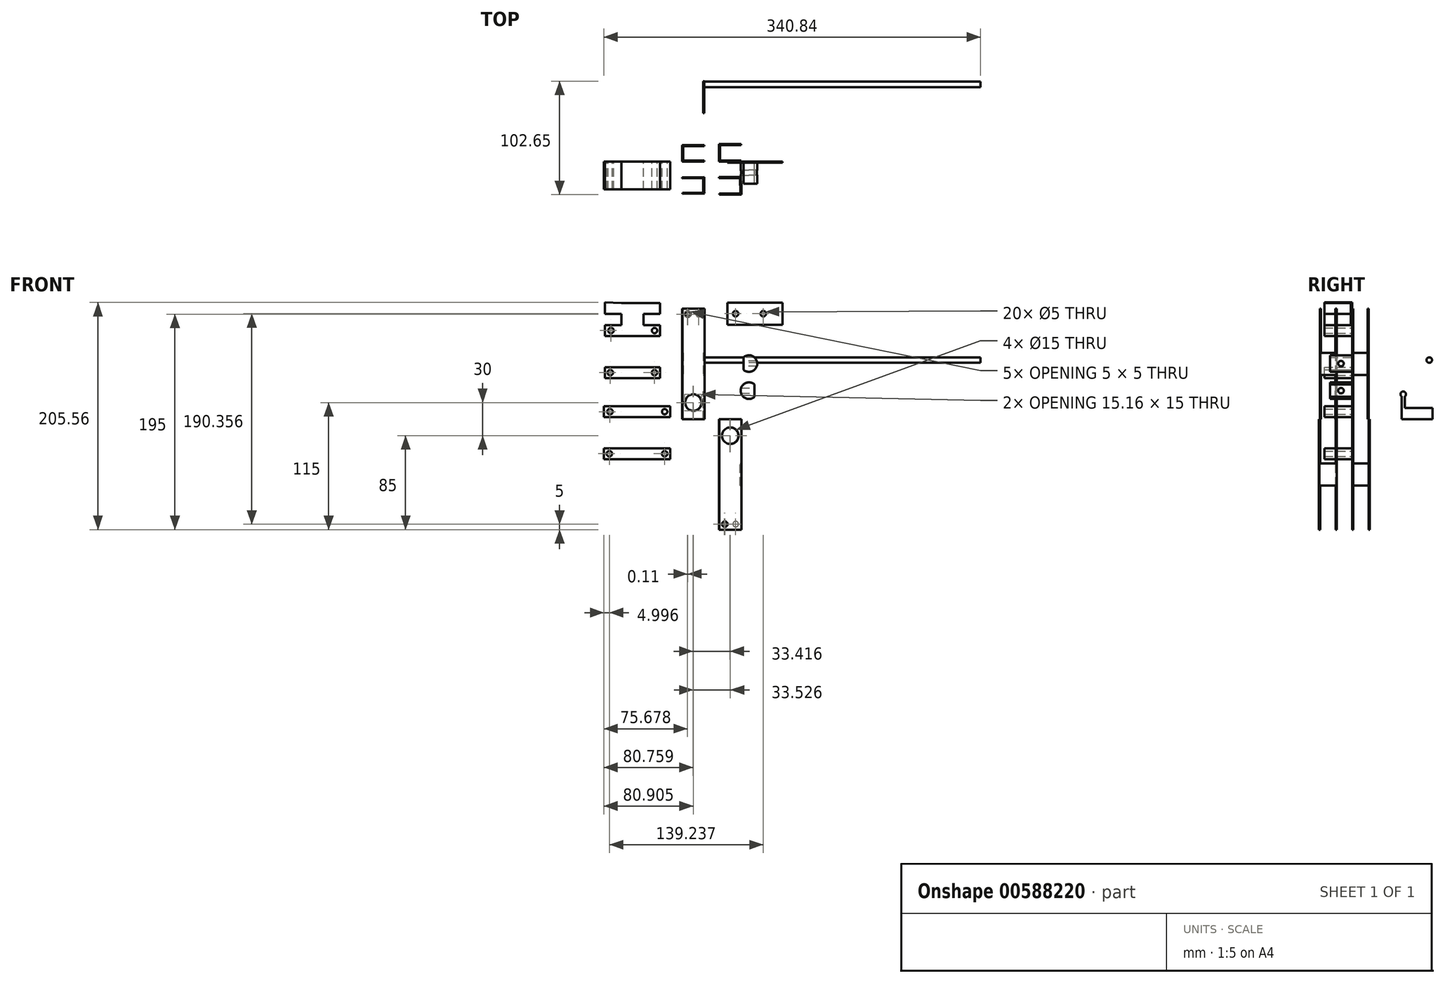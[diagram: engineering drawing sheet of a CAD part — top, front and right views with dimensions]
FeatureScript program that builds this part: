
annotation { "Feature Type Name" : "Feature", "Feature Type Description" : "" }
export const myFeature = defineFeature(function(context is Context, id is Id, definition is map)
    precondition{}
    {
        {
            var Q0;
            Q0=qCreatedBy(makeId("Top.planeOp"),FACE);
            var sketch = newSketch(context, id + "F0", { "sketchPlane" : qUnion([Q0])});
            skLineSegment(sketch, "E0", {"start": v(0, 15) * mm, "end": v(-20, 15) * mm});
            skLineSegment(sketch, "E1", {"start": v(-20, 15) * mm, "end": v(-20, 0) * mm});
            skLineSegment(sketch, "E2", {"start": v(-20, 0) * mm, "end": v(0, 0) * mm});
            skLineSegment(sketch, "E3", {"start": v(0, 0) * mm, "end": v(0, 1) * mm});
            skLineSegment(sketch, "E4", {"start": v(0, 1) * mm, "end": v(-19, 1) * mm});
            skLineSegment(sketch, "E5", {"start": v(-19, 1) * mm, "end": v(-19, 14) * mm});
            skLineSegment(sketch, "E6", {"start": v(-19, 14) * mm, "end": v(0, 14) * mm});
            skLineSegment(sketch, "E7", {"start": v(0, 14) * mm, "end": v(0, 15) * mm});
            skLineSegment(sketch, "E8", {"start": v(33.42, 1) * mm, "end": v(14.42, 1) * mm});
            skLineSegment(sketch, "E9", {"start": v(14.42, 1) * mm, "end": v(14.42, 15) * mm});
            skLineSegment(sketch, "E10", {"start": v(14.42, 15) * mm, "end": v(33.42, 15) * mm});
            skLineSegment(sketch, "E11", {"start": v(33.42, 15) * mm, "end": v(33.42, 16) * mm});
            skLineSegment(sketch, "E12", {"start": v(33.42, 16) * mm, "end": v(13.42, 16) * mm});
            skLineSegment(sketch, "E13", {"start": v(13.42, 16) * mm, "end": v(13.42, 0) * mm});
            skLineSegment(sketch, "E14", {"start": v(13.42, 0) * mm, "end": v(33.42, 0) * mm});
            skLineSegment(sketch, "E15", {"start": v(33.42, 0) * mm, "end": v(33.42, 1) * mm});
            skLineSegment(sketch, "E16", {"start": v(-36.62, -7.13) * mm, "end": v(38.64, -6.85) * mm, "construction": true});
            skLineSegment(sketch, "E17.MirrorCS", {"start": v(-19, 16) * mm, "end": v(0, 16) * mm});
            skLineSegment(sketch, "E18.MirrorCS", {"start": v(-19.95, -14.13) * mm, "end": v(0.05, -13.99) * mm});
            skLineSegment(sketch, "E19.MirrorCS", {"start": v(0.16, -28.99) * mm, "end": v(-19.84, -29.13) * mm});
            skLineSegment(sketch, "E20.MirrorCS", {"start": v(13.47, -13.89) * mm, "end": v(33.47, -13.74) * mm});
            skLineSegment(sketch, "E21.MirrorCS", {"start": v(33.58, -29.74) * mm, "end": v(13.58, -29.89) * mm});
            skLineSegment(sketch, "E22", {"start": v(13.47, -13.89) * mm, "end": v(13.47, -14.89) * mm});
            skLineSegment(sketch, "E23", {"start": v(13.47, -14.89) * mm, "end": v(32.47, -14.75) * mm});
            skLineSegment(sketch, "E24", {"start": v(32.58, -28.75) * mm, "end": v(13.58, -28.89) * mm});
            skLineSegment(sketch, "E25", {"start": v(13.58, -28.89) * mm, "end": v(13.58, -29.89) * mm});
            skLineSegment(sketch, "E26", {"start": v(32.58, -28.75) * mm, "end": v(32.47, -14.75) * mm});
            skLineSegment(sketch, "E27", {"start": v(33.47, -13.74) * mm, "end": v(33.58, -29.74) * mm});
            skLineSegment(sketch, "E28", {"start": v(0.05, -13.99) * mm, "end": v(0.16, -28.99) * mm});
            skLineSegment(sketch, "E29", {"start": v(-19.95, -14.13) * mm, "end": v(-19.94, -15.13) * mm});
            skLineSegment(sketch, "E30", {"start": v(-19.94, -15.13) * mm, "end": v(-0.94, -15) * mm});
            skLineSegment(sketch, "E31", {"start": v(-0.94, -15) * mm, "end": v(-0.85, -28) * mm});
            skLineSegment(sketch, "E32", {"start": v(-0.85, -28) * mm, "end": v(-19.84, -28.13) * mm});
            skLineSegment(sketch, "E33", {"start": v(-19.84, -29.13) * mm, "end": v(-19.84, -28.13) * mm});
            skSolve(sketch);
        }
        {
            var Q0;
            Q0=makeQuery(id+"F0.imprint","IMPRINT",FACE,{"disambiguationData":[TD([[makeQuery(id+"F0.imprint","IMPRINT",EDGE,{"derivedFrom":sQuery(id+"F0.wireOp",EDGE,"E0")}),1.0]])]});
            var Q1;
            Q1=makeQuery(id+"F0.imprint","IMPRINT",FACE,{"disambiguationData":[TD([[makeQuery(id+"F0.imprint","IMPRINT",EDGE,{"derivedFrom":sQuery(id+"F0.wireOp",EDGE,"E19.MirrorCS")}),-1.0]])]});
            extrude(context, id + "F1", {"entities" : qUnion([Q0, Q1]), "depth" : 100 * mm, "offsetDistance" : 25 * mm});
        }
        {
            var Q0;
            Q0=makeQuery(id+"F1.opExtrude","SWEPT_FACE",FACE,{"disambiguationData":[OSD([sQuery(id+"F0.wireOp",EDGE,"E2")])]});
            var sketch = newSketch(context, id + "F2", { "sketchPlane" : qUnion([Q0])});
            skCircle(sketch, "E34", {"center": v(-10, 15) * mm, "radius": 7.5 * mm});
            skPoint(sketch, "E34.centerSnap0", {"position": v(-10, 0) * mm});
            skCircle(sketch, "E35", {"center": v(-5, 95) * mm, "radius": 2.5 * mm});
            skSolve(sketch);
        }
        {
            var Q0;
            Q0=makeQuery(id+"F2.imprint","IMPRINT",FACE,{"disambiguationData":[TD([[makeQuery(id+"F2.imprint","IMPRINT",EDGE,{"derivedFrom":sQuery(id+"F2.wireOp",EDGE,"E34")}),1.0]])]});
            var Q1;
            Q1=makeQuery(id+"F2.imprint","IMPRINT",FACE,{"disambiguationData":[TD([[makeQuery(id+"F2.imprint","IMPRINT",EDGE,{"derivedFrom":sQuery(id+"F2.wireOp",EDGE,"E35")}),1.0]])]});
            extrude(context, id + "F3", {"entities" : qUnion([Q0, Q1]), "operationType" : NewBodyOperationType.REMOVE, "endBound" : BoundingType.THROUGH_ALL, "oppositeDirection" : true, "depth" : 25 * mm, "offsetDistance" : 25 * mm});
        }
        {
            var Q0;
            Q0=makeQuery(id+"F1.opExtrude","SWEPT_FACE",FACE,{"disambiguationData":[OSD([sQuery(id+"F0.wireOp",EDGE,"E1")])]});
            var sketch = newSketch(context, id + "F4", { "sketchPlane" : qUnion([Q0])});
            skPoint(sketch, "E36.centerSnap0", {"position": v(-7.5, 0) * mm});
            skLineSegment(sketch, "E37", {"start": v(-14, 0) * mm, "end": v(-14, 40) * mm});
            skLineSegment(sketch, "E38", {"start": v(-14, 40) * mm, "end": v(-1, 40) * mm});
            skLineSegment(sketch, "E39", {"start": v(-1, 40) * mm, "end": v(-1, 0) * mm});
            skLineSegment(sketch, "E40", {"start": v(-14, 100) * mm, "end": v(-14, 60) * mm});
            skLineSegment(sketch, "E41", {"start": v(-14, 60) * mm, "end": v(-1, 60) * mm});
            skLineSegment(sketch, "E42", {"start": v(-1, 60) * mm, "end": v(-1, 100) * mm});
            skSolve(sketch);
        }
        {
            var Q0;
            {var subQ0=sQuery(id+"F4.wireOp",EDGE,"E37");Q0=makeQuery(id+"F4.imprint","IMPRINT",FACE,{"disambiguationData":[TD([[makeQuery(id+"F4.imprint","IMPRINT",EDGE,{"derivedFrom":subQ0}),-1.0]])]});}
            var Q1;
            {var subQ0=sQuery(id+"F4.wireOp",EDGE,"E40");Q1=makeQuery(id+"F4.imprint","IMPRINT",FACE,{"disambiguationData":[TD([[makeQuery(id+"F4.imprint","IMPRINT",EDGE,{"derivedFrom":subQ0}),1.0]])]});}
            extrude(context, id + "F5", {"entities" : qUnion([Q0, Q1]), "operationType" : NewBodyOperationType.REMOVE, "endBound" : BoundingType.THROUGH_ALL, "oppositeDirection" : true, "depth" : 25 * mm, "offsetDistance" : 25 * mm});
        }
        {
            var Q0;
            Q0=makeQuery(id+"F0.imprint","IMPRINT",FACE,{"disambiguationData":[TD([[makeQuery(id+"F0.imprint","IMPRINT",EDGE,{"derivedFrom":sQuery(id+"F0.wireOp",EDGE,"E8")}),1.0]])]});
            var Q1;
            Q1=makeQuery(id+"F0.imprint","IMPRINT",FACE,{"disambiguationData":[TD([[makeQuery(id+"F0.imprint","IMPRINT",EDGE,{"derivedFrom":sQuery(id+"F0.wireOp",EDGE,"E20.MirrorCS")}),-1.0]])]});
            extrude(context, id + "F6", {"entities" : qUnion([Q0, Q1]), "oppositeDirection" : true, "depth" : 100 * mm, "offsetDistance" : 25 * mm});
        }
        {
            var Q0;
            Q0=makeQuery(id+"F6.opExtrude","SWEPT_FACE",FACE,{"disambiguationData":[OSD([sQuery(id+"F0.wireOp",EDGE,"E14")])]});
            var sketch = newSketch(context, id + "F7", { "sketchPlane" : qUnion([Q0])});
            skCircle(sketch, "E43", {"center": v(23.42, -15) * mm, "radius": 7.5 * mm});
            skPoint(sketch, "E43.centerSnap0", {"position": v(23.42, 0) * mm});
            skCircle(sketch, "E44", {"center": v(28.42, -95) * mm, "radius": 2.5 * mm});
            skSolve(sketch);
        }
        {
            var Q0;
            Q0=makeQuery(id+"F7.imprint","IMPRINT",FACE,{"disambiguationData":[TD([[makeQuery(id+"F7.imprint","IMPRINT",EDGE,{"derivedFrom":sQuery(id+"F7.wireOp",EDGE,"E43")}),1.0]])]});
            var Q1;
            Q1=makeQuery(id+"F7.imprint","IMPRINT",FACE,{"disambiguationData":[TD([[makeQuery(id+"F7.imprint","IMPRINT",EDGE,{"derivedFrom":sQuery(id+"F7.wireOp",EDGE,"E44")}),1.0]])]});
            extrude(context, id + "F8", {"entities" : qUnion([Q0, Q1]), "operationType" : NewBodyOperationType.REMOVE, "endBound" : BoundingType.THROUGH_ALL, "oppositeDirection" : true, "depth" : 25 * mm, "offsetDistance" : 25 * mm});
        }
        {
            var Q0;
            Q0=makeQuery(id+"F6.opExtrude","SWEPT_FACE",FACE,{"disambiguationData":[OSD([sQuery(id+"F0.wireOp",EDGE,"E13")])]});
            var sketch = newSketch(context, id + "F9", { "sketchPlane" : qUnion([Q0])});
            skLineSegment(sketch, "E45", {"start": v(-15, 0) * mm, "end": v(-15, -40) * mm});
            skLineSegment(sketch, "E46", {"start": v(-15, -40) * mm, "end": v(-1, -40) * mm});
            skLineSegment(sketch, "E47", {"start": v(-1, -40) * mm, "end": v(-1, 0) * mm});
            skLineSegment(sketch, "E48", {"start": v(-15, -100) * mm, "end": v(-15, -60) * mm});
            skLineSegment(sketch, "E49", {"start": v(-15, -60) * mm, "end": v(-1, -60) * mm});
            skLineSegment(sketch, "E50", {"start": v(-1, -60) * mm, "end": v(-1, -100) * mm});
            skSolve(sketch);
        }
        {
            var Q0;
            {var subQ0=sQuery(id+"F9.wireOp",EDGE,"E45");Q0=makeQuery(id+"F9.imprint","IMPRINT",FACE,{"disambiguationData":[TD([[makeQuery(id+"F9.imprint","IMPRINT",EDGE,{"derivedFrom":subQ0}),1.0]])]});}
            var Q1;
            {var subQ0=sQuery(id+"F9.wireOp",EDGE,"E48");Q1=makeQuery(id+"F9.imprint","IMPRINT",FACE,{"disambiguationData":[TD([[makeQuery(id+"F9.imprint","IMPRINT",EDGE,{"derivedFrom":subQ0}),-1.0]])]});}
            extrude(context, id + "F10", {"entities" : qUnion([Q0, Q1]), "operationType" : NewBodyOperationType.REMOVE, "endBound" : BoundingType.THROUGH_ALL, "oppositeDirection" : true, "depth" : 25 * mm, "offsetDistance" : 25 * mm});
        }
        {
            var Q0;
            Q0=qCreatedBy(makeId("Front.planeOp"),FACE);
            var sketch = newSketch(context, id + "F11", { "sketchPlane" : qUnion([Q0])});
            skLineSegment(sketch, "E51.bottom", {"start": v(20.9, 105.36) * mm, "end": v(70.9, 105.36) * mm});
            skLineSegment(sketch, "E51.top", {"start": v(20.9, 85.36) * mm, "end": v(70.9, 85.36) * mm});
            skLineSegment(sketch, "E51.left", {"start": v(20.9, 105.36) * mm, "end": v(20.9, 85.36) * mm});
            skLineSegment(sketch, "E51.right", {"start": v(70.9, 105.36) * mm, "end": v(70.9, 85.36) * mm});
            skCircle(sketch, "E52", {"center": v(28.4, 95.36) * mm, "radius": 2.5 * mm});
            skPoint(sketch, "E52.centerSnap0", {"position": v(20.9, 95.36) * mm});
            skCircle(sketch, "E53.MirrorC", {"center": v(53.4, 95.36) * mm, "radius": 2.5 * mm});
            skSolve(sketch);
        }
        {
            var Q0;
            Q0=makeQuery(id+"F11.imprint","IMPRINT",FACE,{"disambiguationData":[TD([[makeQuery(id+"F11.imprint","IMPRINT",EDGE,{"derivedFrom":sQuery(id+"F11.wireOp",EDGE,"E51.bottom")}),-1.0]])]});
            extrude(context, id + "F12", {"entities" : qUnion([Q0]), "depth" : 1 * mm, "offsetDistance" : 25 * mm});
        }
        {
            var Q0;
            Q0=makeQuery(id+"F1.opExtrude","SWEPT_FACE",FACE,{"disambiguationData":[OSD([sQuery(id+"F0.wireOp",EDGE,"E19.MirrorCS")])]});
            var sketch = newSketch(context, id + "F13", { "sketchPlane" : qUnion([Q0])});
            skCircle(sketch, "E54", {"center": v(-15.05, 95) * mm, "radius": 2.5 * mm});
            skCircle(sketch, "E55", {"center": v(-10.05, 15) * mm, "radius": 7.5 * mm});
            skPoint(sketch, "E55.centerSnap0", {"position": v(-10.05, 0) * mm});
            skSolve(sketch);
        }
        {
            var Q0;
            Q0=makeQuery(id+"F13.imprint","IMPRINT",FACE,{"disambiguationData":[TD([[makeQuery(id+"F13.imprint","IMPRINT",EDGE,{"derivedFrom":sQuery(id+"F13.wireOp",EDGE,"E54")}),1.0]])]});
            var Q1;
            Q1=makeQuery(id+"F13.imprint","IMPRINT",FACE,{"disambiguationData":[TD([[makeQuery(id+"F13.imprint","IMPRINT",EDGE,{"derivedFrom":sQuery(id+"F13.wireOp",EDGE,"E55")}),1.0]])]});
            extrude(context, id + "F14", {"entities" : qUnion([Q0, Q1]), "operationType" : NewBodyOperationType.REMOVE, "endBound" : BoundingType.THROUGH_ALL, "oppositeDirection" : true, "depth" : 25 * mm, "offsetDistance" : 25 * mm});
        }
        {
            var Q0;
            Q0=makeQuery(id+"F6.opExtrude","SWEPT_FACE",FACE,{"disambiguationData":[OSD([sQuery(id+"F0.wireOp",EDGE,"E21.MirrorCS")])]});
            var sketch = newSketch(context, id + "F15", { "sketchPlane" : qUnion([Q0])});
            skCircle(sketch, "E56", {"center": v(23.36, -15) * mm, "radius": 7.5 * mm});
            skPoint(sketch, "E56.centerSnap0", {"position": v(23.36, 0) * mm});
            skCircle(sketch, "E57", {"center": v(18.36, -95) * mm, "radius": 2.5 * mm});
            skSolve(sketch);
        }
        {
            var Q0;
            Q0=qSketchRegion(id+"F15",true);
            extrude(context, id + "F16", {"entities" : qUnion([Q0]), "operationType" : NewBodyOperationType.REMOVE, "endBound" : BoundingType.THROUGH_ALL, "oppositeDirection" : true, "depth" : 25 * mm, "offsetDistance" : 25 * mm});
        }
        {
            var Q0;
            Q0=makeQuery(id+"F6.opExtrude","SWEPT_FACE",FACE,{"disambiguationData":[OSD([sQuery(id+"F0.wireOp",EDGE,"E27")])]});
            var sketch = newSketch(context, id + "F17", { "sketchPlane" : qUnion([Q0])});
            skLineSegment(sketch, "E58", {"start": v(-14.99, -40) * mm, "end": v(-28.99, -40) * mm});
            skLineSegment(sketch, "E59", {"start": v(-28.99, -40) * mm, "end": v(-28.99, 0) * mm});
            skLineSegment(sketch, "E60", {"start": v(-14.99, -40) * mm, "end": v(-14.99, 0) * mm});
            skLineSegment(sketch, "E61", {"start": v(-28.99, -100) * mm, "end": v(-28.99, -60) * mm});
            skLineSegment(sketch, "E62", {"start": v(-28.99, -60) * mm, "end": v(-14.99, -60) * mm});
            skLineSegment(sketch, "E63", {"start": v(-14.99, -60) * mm, "end": v(-14.99, -100) * mm});
            skSolve(sketch);
        }
        {
            var Q0;
            Q0=makeQuery(id+"F17.imprint","IMPRINT",FACE,{"disambiguationData":[TD([[makeQuery(id+"F17.imprint","IMPRINT",EDGE,{"derivedFrom":sQuery(id+"F17.wireOp",EDGE,"E58")}),-1.0]])]});
            var Q1;
            {var subQ0=sQuery(id+"F17.wireOp",EDGE,"E61");Q1=makeQuery(id+"F17.imprint","IMPRINT",FACE,{"disambiguationData":[TD([[makeQuery(id+"F17.imprint","IMPRINT",EDGE,{"derivedFrom":subQ0}),-1.0]])]});}
            extrude(context, id + "F18", {"entities" : qUnion([Q0, Q1]), "operationType" : NewBodyOperationType.REMOVE, "endBound" : BoundingType.THROUGH_ALL, "oppositeDirection" : true, "depth" : 25 * mm, "offsetDistance" : 25 * mm});
        }
        {
            var Q0;
            Q0=makeQuery(id+"F1.opExtrude","SWEPT_FACE",FACE,{"disambiguationData":[OSD([sQuery(id+"F0.wireOp",EDGE,"E28")])]});
            var sketch = newSketch(context, id + "F19", { "sketchPlane" : qUnion([Q0])});
            skLineSegment(sketch, "E64", {"start": v(-14.99, 0) * mm, "end": v(-14.99, 40) * mm});
            skLineSegment(sketch, "E65", {"start": v(-14.99, 40) * mm, "end": v(-27.99, 40) * mm});
            skLineSegment(sketch, "E66", {"start": v(-27.99, 40) * mm, "end": v(-27.99, 0) * mm});
            skLineSegment(sketch, "E67", {"start": v(-27.99, 100) * mm, "end": v(-27.99, 60) * mm});
            skLineSegment(sketch, "E68", {"start": v(-27.99, 60) * mm, "end": v(-14.99, 60) * mm});
            skLineSegment(sketch, "E69", {"start": v(-14.99, 60) * mm, "end": v(-14.99, 100) * mm});
            skSolve(sketch);
        }
        {
            var Q0;
            {var subQ0=sQuery(id+"F19.wireOp",EDGE,"E64");Q0=makeQuery(id+"F19.imprint","IMPRINT",FACE,{"disambiguationData":[TD([[makeQuery(id+"F19.imprint","IMPRINT",EDGE,{"derivedFrom":subQ0}),1.0]])]});}
            var Q1;
            {var subQ0=sQuery(id+"F19.wireOp",EDGE,"E67");Q1=makeQuery(id+"F19.imprint","IMPRINT",FACE,{"disambiguationData":[TD([[makeQuery(id+"F19.imprint","IMPRINT",EDGE,{"derivedFrom":subQ0}),1.0]])]});}
            extrude(context, id + "F20", {"entities" : qUnion([Q0, Q1]), "operationType" : NewBodyOperationType.REMOVE, "oppositeDirection" : true, "depth" : 25 * mm, "offsetDistance" : 25 * mm});
        }
        {
            var Q0;
            Q0=qCreatedBy(makeId("Front.planeOp"),FACE);
            var sketch = newSketch(context, id + "F21", { "sketchPlane" : qUnion([Q0])});
            skArc(sketch, "E70", {"start": v(35.49, 44.6) * mm, "mid": v(47.93, 50.24) * mm, "end": v(35.49, 55.88) * mm});
            skArc(sketch, "E71", {"start": v(45.38, 31.4) * mm, "mid": v(32.93, 25.77) * mm, "end": v(45.38, 20.13) * mm});
            skLineSegment(sketch, "E72", {"start": v(35.49, 55.88) * mm, "end": v(35.49, 44.6) * mm});
            skLineSegment(sketch, "E73.trimOffspring", {"start": v(45.38, 31.4) * mm, "end": v(45.38, 20.13) * mm});
            skPoint(sketch, "E74.orphan", {"position": v(40.43, 57.74) * mm});
            skSolve(sketch);
        }
        {
            var Q0;
            Q0=makeQuery(id+"F21.imprint","IMPRINT",FACE,{"disambiguationData":[TD([[makeQuery(id+"F21.imprint","IMPRINT",EDGE,{"derivedFrom":sQuery(id+"F21.wireOp",EDGE,"E70")}),1.0]])]});
            var Q1;
            Q1=makeQuery(id+"F21.imprint","IMPRINT",FACE,{"disambiguationData":[TD([[makeQuery(id+"F21.imprint","IMPRINT",EDGE,{"derivedFrom":sQuery(id+"F21.wireOp",EDGE,"E71")}),1.0]])]});
            extrude(context, id + "F22", {"entities" : qUnion([Q0, Q1]), "depth" : 20 * mm, "offsetDistance" : 25 * mm});
        }
        {
            var Q0;
            Q0=qCreatedBy(makeId("Right.planeOp"),FACE);
            var sketch = newSketch(context, id + "F23", { "sketchPlane" : qUnion([Q0])});
            skCircle(sketch, "E75", {"center": v(69.88, 53.43) * mm, "radius": 2.5 * mm});
            skSolve(sketch);
        }
        {
            var Q0;
            Q0=makeQuery(id+"F23.imprint","IMPRINT",FACE,{"disambiguationData":[TD([[makeQuery(id+"F23.imprint","IMPRINT",EDGE,{"derivedFrom":sQuery(id+"F23.wireOp",EDGE,"E75")}),1.0]])]});
            extrude(context, id + "F24", {"entities" : qUnion([Q0]), "depth" : 250 * mm, "offsetDistance" : 25 * mm});
        }
        {
            var Q0;
            Q0=qCreatedBy(makeId("Front.planeOp"),FACE);
            var sketch = newSketch(context, id + "F25", { "sketchPlane" : qUnion([Q0])});
            skLineSegment(sketch, "E76.top", {"start": v(-89.95, 75.12) * mm, "end": v(-39.95, 75.12) * mm});
            skLineSegment(sketch, "E76.left", {"start": v(-89.95, 85.12) * mm, "end": v(-89.95, 75.12) * mm});
            skLineSegment(sketch, "E76.right", {"start": v(-39.95, 85.12) * mm, "end": v(-39.95, 75.12) * mm});
            skCircle(sketch, "E77", {"center": v(-84.38, 80.12) * mm, "radius": 2.5 * mm});
            skPoint(sketch, "E77.centerSnap0", {"position": v(-89.95, 80.12) * mm});
            skCircle(sketch, "E78", {"center": v(-44.95, 80.12) * mm, "radius": 2.41 * mm});
            skPoint(sketch, "E78.centerSnap0", {"position": v(-39.95, 80.12) * mm});
            skLineSegment(sketch, "E79.MirrorCS", {"start": v(-89.95, 47.06) * mm, "end": v(-39.95, 47.06) * mm});
            skLineSegment(sketch, "E80.MirrorCS", {"start": v(-89.95, 37.06) * mm, "end": v(-89.95, 47.06) * mm});
            skLineSegment(sketch, "E81.MirrorCS", {"start": v(-89.95, 37.06) * mm, "end": v(-39.95, 37.06) * mm});
            skLineSegment(sketch, "E82.MirrorCS", {"start": v(-39.95, 37.06) * mm, "end": v(-39.95, 47.06) * mm});
            skCircle(sketch, "E83", {"center": v(-84.95, 42.06) * mm, "radius": 2.5 * mm});
            skPoint(sketch, "E83.centerSnap0", {"position": v(-89.95, 42.06) * mm});
            skCircle(sketch, "E84", {"center": v(-44.95, 42.06) * mm, "radius": 2.5 * mm});
            skPoint(sketch, "E84.centerSnap0", {"position": v(-39.95, 42.06) * mm});
            skLineSegment(sketch, "E85.bottom", {"start": v(-90.84, 11.74) * mm, "end": v(-30.84, 11.74) * mm});
            skLineSegment(sketch, "E85.top", {"start": v(-90.84, 1.74) * mm, "end": v(-30.84, 1.74) * mm});
            skLineSegment(sketch, "E85.left", {"start": v(-90.84, 11.74) * mm, "end": v(-90.84, 1.74) * mm});
            skLineSegment(sketch, "E85.right", {"start": v(-30.84, 11.74) * mm, "end": v(-30.84, 1.74) * mm});
            skCircle(sketch, "E86", {"center": v(-85.27, 6.74) * mm, "radius": 2.5 * mm});
            skPoint(sketch, "E86.centerSnap0", {"position": v(-90.84, 6.74) * mm});
            skCircle(sketch, "E87", {"center": v(-35.84, 6.74) * mm, "radius": 2.41 * mm});
            skPoint(sketch, "E87.centerSnap0", {"position": v(-30.84, 6.74) * mm});
            skLineSegment(sketch, "E88.MirrorCS", {"start": v(-90.84, -36.32) * mm, "end": v(-90.84, -26.32) * mm});
            skLineSegment(sketch, "E89.MirrorCS", {"start": v(-30.84, -36.32) * mm, "end": v(-30.84, -26.32) * mm});
            skCircle(sketch, "E90", {"center": v(-85.84, -31.32) * mm, "radius": 2.5 * mm});
            skPoint(sketch, "E90.centerSnap0", {"position": v(-90.84, -31.32) * mm});
            skCircle(sketch, "E91", {"center": v(-35.84, -31.32) * mm, "radius": 2.5 * mm});
            skPoint(sketch, "E91.centerSnap0", {"position": v(-30.84, -31.32) * mm});
            skLineSegment(sketch, "E92", {"start": v(-90.84, -26.32) * mm, "end": v(-30.84, -26.32) * mm});
            skLineSegment(sketch, "E93", {"start": v(-90.84, -36.32) * mm, "end": v(-30.84, -36.32) * mm});
            skLineSegment(sketch, "E94", {"start": v(-74.95, 85.12) * mm, "end": v(-74.95, 95.12) * mm});
            skLineSegment(sketch, "E95", {"start": v(-74.95, 105.12) * mm, "end": v(-64.95, 105.12) * mm});
            skLineSegment(sketch, "E96.MirrorCS", {"start": v(-54.95, 85.12) * mm, "end": v(-54.95, 95.12) * mm});
            skLineSegment(sketch, "E97.MirrorCS", {"start": v(-54.95, 105.12) * mm, "end": v(-64.95, 105.12) * mm});
            skLineSegment(sketch, "E98.MirrorCS", {"start": v(-89.95, 135.12) * mm, "end": v(-39.95, 135.12) * mm});
            skLineSegment(sketch, "E99.MirrorCS", {"start": v(-89.95, 85.12) * mm, "end": v(-74.95, 85.12) * mm});
            skLineSegment(sketch, "E100", {"start": v(-89.95, 95.12) * mm, "end": v(-89.95, 105.56) * mm});
            skLineSegment(sketch, "E101", {"start": v(-89.95, 105.56) * mm, "end": v(-74.95, 105.12) * mm});
            skLineSegment(sketch, "E102", {"start": v(-54.95, 105.12) * mm, "end": v(-39.95, 105.12) * mm});
            skLineSegment(sketch, "E103", {"start": v(-39.95, 105.12) * mm, "end": v(-39.95, 95.12) * mm});
            skLineSegment(sketch, "E104.trimOffspring", {"start": v(-54.95, 95.12) * mm, "end": v(-39.95, 95.12) * mm});
            skLineSegment(sketch, "E105", {"start": v(-74.95, 95.12) * mm, "end": v(-89.95, 95.12) * mm});
            skLineSegment(sketch, "E106.trimOffspring", {"start": v(-54.95, 85.12) * mm, "end": v(-39.95, 85.12) * mm});
            skPoint(sketch, "E107.end.orphan", {"position": v(-64.95, 75.12) * mm});
            skPoint(sketch, "E107.start.orphan", {"position": v(-64.95, 85.12) * mm});
            skSolve(sketch);
        }
        {
            var Q0;
            Q0=makeQuery(id+"F25.imprint","IMPRINT",FACE,{"disambiguationData":[TD([[makeQuery(id+"F25.imprint","IMPRINT",EDGE,{"derivedFrom":sQuery(id+"F25.wireOp",EDGE,"E76.bottom")}),-1.0]])]});
            var Q1;
            {var subQ2=sQuery(id+"F25.wireOp",EDGE,"E80.MirrorCS");Q1=makeQuery(id+"F25.imprint","IMPRINT",FACE,{"disambiguationData":[TD([[makeQuery(id+"F25.imprint","IMPRINT",EDGE,{"derivedFrom":subQ2}),-1.0]])]});}
            var Q2;
            Q2=makeQuery(id+"F25.imprint","IMPRINT",FACE,{"disambiguationData":[TD([[makeQuery(id+"F25.imprint","IMPRINT",EDGE,{"derivedFrom":sQuery(id+"F25.wireOp",EDGE,"E76.top")}),1.0]])]});
            extrude(context, id + "F26", {"entities" : qUnion([Q0, Q1, Q2]), "depth" : 25 * mm, "offsetDistance" : 25 * mm});
        }
        {
            var Q0;
            Q0=makeQuery(id+"F25.imprint","IMPRINT",FACE,{"disambiguationData":[TD([[makeQuery(id+"F25.imprint","IMPRINT",EDGE,{"derivedFrom":sQuery(id+"F25.wireOp",EDGE,"E88.MirrorCS")}),-1.0]])]});
            var Q1;
            Q1=makeQuery(id+"F25.imprint","IMPRINT",FACE,{"disambiguationData":[TD([[makeQuery(id+"F25.imprint","IMPRINT",EDGE,{"derivedFrom":sQuery(id+"F25.wireOp",EDGE,"E85.bottom")}),-1.0]])]});
            extrude(context, id + "F27", {"entities" : qUnion([Q0, Q1]), "depth" : 25 * mm, "offsetDistance" : 25 * mm});
        }
        {
            var Q0;
            Q0=makeQuery(id+"F22.opExtrude","SWEPT_FACE",FACE,{"disambiguationData":[OSD([sQuery(id+"F21.wireOp",EDGE,"E73.trimOffspring")])]});
            var sketch = newSketch(context, id + "F28", { "sketchPlane" : qUnion([Q0])});
            skCircle(sketch, "E108", {"center": v(-10, 25.77) * mm, "radius": 2.5 * mm});
            skPoint(sketch, "E108.centerSnap0", {"position": v(-20, 25.77) * mm});
            skPoint(sketch, "E108.centerSnap1", {"position": v(-10, 31.4) * mm});
            skSolve(sketch);
        }
        {
            var Q0;
            Q0=makeQuery(id+"F28.imprint","IMPRINT",FACE,{"disambiguationData":[TD([[makeQuery(id+"F28.imprint","IMPRINT",EDGE,{"derivedFrom":sQuery(id+"F28.wireOp",EDGE,"E108")}),1.0]])]});
            extrude(context, id + "F29", {"entities" : qUnion([Q0]), "operationType" : NewBodyOperationType.REMOVE, "endBound" : BoundingType.THROUGH_ALL, "oppositeDirection" : true, "depth" : 25 * mm, "offsetDistance" : 25 * mm});
        }
        {
            var Q0;
            Q0=makeQuery(id+"F22.opExtrude","SWEPT_FACE",FACE,{"disambiguationData":[OSD([sQuery(id+"F21.wireOp",EDGE,"E72")])]});
            var sketch = newSketch(context, id + "F30", { "sketchPlane" : qUnion([Q0])});
            skCircle(sketch, "E109", {"center": v(10, 50.24) * mm, "radius": 2.5 * mm});
            skPoint(sketch, "E109.centerSnap0", {"position": v(10, 44.6) * mm});
            skPoint(sketch, "E109.centerSnap1", {"position": v(0, 50.24) * mm});
            skSolve(sketch);
        }
        {
            var Q0;
            Q0=makeQuery(id+"F30.imprint","IMPRINT",FACE,{"disambiguationData":[TD([[makeQuery(id+"F30.imprint","IMPRINT",EDGE,{"derivedFrom":sQuery(id+"F30.wireOp",EDGE,"E109")}),1.0]])]});
            extrude(context, id + "F31", {"entities" : qUnion([Q0]), "operationType" : NewBodyOperationType.REMOVE, "endBound" : BoundingType.THROUGH_ALL, "oppositeDirection" : true, "depth" : 25 * mm, "offsetDistance" : 25 * mm});
        }
        {
            var Q0;
            Q0=qCreatedBy(makeId("Right.planeOp"),FACE);
            var sketch = newSketch(context, id + "F32", { "sketchPlane" : qUnion([Q0])});
            skArc(sketch, "E110", {"start": v(47.76, 20.47) * mm, "mid": v(46.3, 25) * mm, "end": v(44.85, 20.47) * mm});
            skLineSegment(sketch, "E111", {"start": v(47.76, 8.68) * mm, "end": v(47.76, 20.47) * mm});
            skLineSegment(sketch, "E112.MirrorCS", {"start": v(44.85, 8.68) * mm, "end": v(44.85, 20.47) * mm});
            skLineSegment(sketch, "E113", {"start": v(37.92, 27.31) * mm, "end": v(57.96, 27.31) * mm, "construction": true});
            skLineSegment(sketch, "E114", {"start": v(44.85, 8.68) * mm, "end": v(44.85, 0) * mm});
            skLineSegment(sketch, "E115", {"start": v(44.85, 0) * mm, "end": v(47.76, 0) * mm});
            skLineSegment(sketch, "E116", {"start": v(47.76, 0) * mm, "end": v(47.76, 8.68) * mm});
            skArc(sketch, "E117.MirrorCS", {"start": v(47.76, 34.16) * mm, "mid": v(46.3, 29.63) * mm, "end": v(44.85, 34.16) * mm});
            skLineSegment(sketch, "E118.MirrorCS", {"start": v(44.85, 45.94) * mm, "end": v(44.85, 34.16) * mm});
            skLineSegment(sketch, "E119.MirrorCS", {"start": v(47.76, 45.94) * mm, "end": v(47.76, 34.16) * mm});
            skLineSegment(sketch, "E120.MirrorCS", {"start": v(44.85, 45.94) * mm, "end": v(44.85, 54.62) * mm});
            skLineSegment(sketch, "E121.MirrorCS", {"start": v(47.76, 54.62) * mm, "end": v(47.76, 45.94) * mm});
            skLineSegment(sketch, "E122.MirrorCS", {"start": v(44.85, 54.62) * mm, "end": v(47.76, 54.62) * mm});
            skSolve(sketch);
        }
        {
            var Q0;
            Q0=makeQuery(id+"F32.imprint","IMPRINT",FACE,{"disambiguationData":[TD([[makeQuery(id+"F32.imprint","IMPRINT",EDGE,{"derivedFrom":sQuery(id+"F32.wireOp",EDGE,"E110")}),1.0]])]});
            var Q1;
            Q1=makeQuery(id+"F32.imprint","IMPRINT",FACE,{"disambiguationData":[TD([[makeQuery(id+"F32.imprint","IMPRINT",EDGE,{"derivedFrom":sQuery(id+"F32.wireOp",EDGE,"E117.MirrorCS")}),-1.0]])]});
            extrude(context, id + "F33", {"entities" : qUnion([Q0, Q1]), "oppositeDirection" : true, "depth" : 1 * mm, "offsetDistance" : 25 * mm});
        }
        {
            var Q0;
            Q0=makeQuery(id+"F33.opExtrude","SWEPT_FACE",FACE,{"disambiguationData":[OSD([sQuery(id+"F32.wireOp",EDGE,"E111"),sQuery(id+"F32.wireOp",EDGE,"E116")])]});
            var sketch = newSketch(context, id + "F34", { "sketchPlane" : qUnion([Q0])});
            skLineSegment(sketch, "E123", {"start": v(0, 10) * mm, "end": v(1, 10) * mm});
            skLineSegment(sketch, "E124", {"start": v(0.98, 44.62) * mm, "end": v(0, 44.62) * mm});
            skSolve(sketch);
        }
        {
            var Q0;
            {var subQ0=sQuery(id+"F34.wireOp",EDGE,"E123");Q0=makeQuery(id+"F34.imprint","IMPRINT",FACE,{"disambiguationData":[TD([[makeQuery(id+"F34.imprint","IMPRINT",EDGE,{"derivedFrom":subQ0}),-1.0]])]});}
            extrude(context, id + "F35", {"entities" : qUnion([Q0]), "operationType" : NewBodyOperationType.ADD, "depth" : 25 * mm, "offsetDistance" : 25 * mm});
        }
    });
